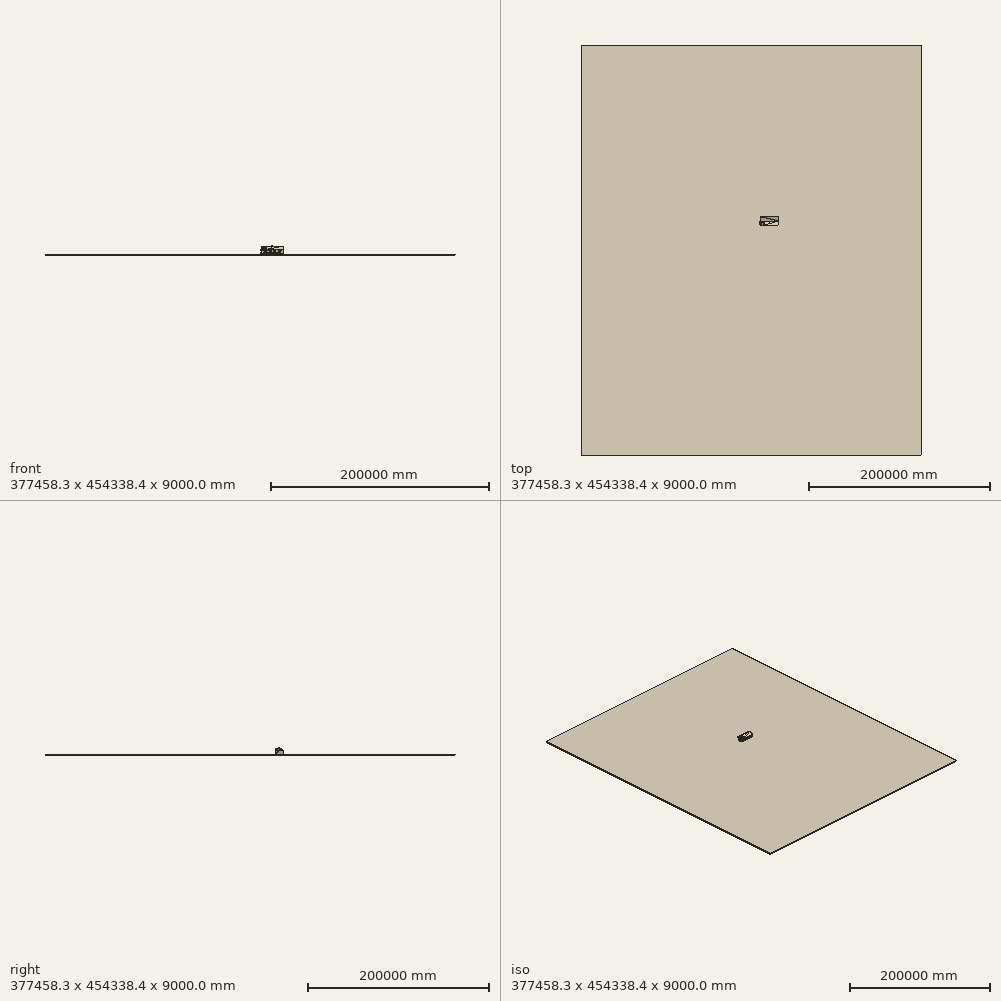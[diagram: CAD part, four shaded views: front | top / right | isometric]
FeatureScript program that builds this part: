
annotation { "Feature Type Name" : "Feature", "Feature Type Description" : "" }
export const myFeature = defineFeature(function(context is Context, id is Id, definition is map)
    precondition{}
    {
        {
            var Q0;
            Q0=qCreatedBy(makeId("Top.planeOp"),FACE);
            var sketch = newSketch(context, id + "F0", { "sketchPlane" : qUnion([Q0])});
            skLineSegment(sketch, "E0.bottom", {"start": v(-10000, 4500) * mm, "end": v(10000, 4500) * mm});
            skLineSegment(sketch, "E0.top", {"start": v(-10000, -4500) * mm, "end": v(10000, -4500) * mm});
            skLineSegment(sketch, "E0.left", {"start": v(-10000, 4500) * mm, "end": v(-10000, -4500) * mm});
            skLineSegment(sketch, "E0.right", {"start": v(10000, 4500) * mm, "end": v(10000, -4500) * mm});
            skLineSegment(sketch, "E1", {"start": v(-10000, 4500) * mm, "end": v(10000, -4500) * mm, "construction": true});
            skSolve(sketch);
        }
        {
            var Q0;
            Q0 = qSketchRegion(id + "F0", true);
            extrude(context, id + "F1", {"entities" : qUnion([Q0]), "depth" : 700 * mm});
        }
        {
            var Q0;
            Q0=qCreatedBy(makeId("Right.planeOp"),FACE);
            var sketch = newSketch(context, id + "F2", { "sketchPlane" : qUnion([Q0])});
            skLineSegment(sketch, "E2", {"start": v(4500, 700) * mm, "end": v(4500, 4201) * mm});
            skLineSegment(sketch, "E3", {"start": v(4500, 4201) * mm, "end": v(0, 7100) * mm});
            skLineSegment(sketch, "E4", {"start": v(0, 7100) * mm, "end": v(-4500, 4201) * mm});
            skLineSegment(sketch, "E5", {"start": v(-4500, 4201) * mm, "end": v(-4500, 700) * mm});
            skLineSegment(sketch, "E6", {"start": v(-4500, 700) * mm, "end": v(4500, 700) * mm});
            skSolve(sketch);
        }
        {
            var Q0;
            Q0 = qSketchRegion(id + "F2", true);
            var Q1;
            Q1=makeQuery(id+"F1.opExtrude","SWEPT_FACE",FACE,{"disambiguationData":[OSD([sQuery(id+"F0.wireOp",EDGE,"E0.right")])]});
            var Q2;
            Q2=makeQuery(id+"F1.opExtrude","SWEPT_FACE",FACE,{"disambiguationData":[OSD([sQuery(id+"F0.wireOp",EDGE,"E0.left")])]});
            extrude(context, id + "F3", {"entities" : qUnion([Q0]), "endBound" : BoundingType.UP_TO_SURFACE, "endBoundEntityFace" : qUnion([Q1]), "depth" : 25 * mm, "hasSecondDirection" : true, "secondDirectionBound" : SecondDirectionBoundingType.UP_TO_SURFACE, "secondDirectionOppositeDirection" : true, "secondDirectionBoundEntityFace" : qUnion([Q2]), "secondDirectionDepth" : 25 * mm});
        }
        {
            var Q0;
            Q0=makeQuery(id+"F3.opExtrude","SWEPT_FACE",FACE,{"disambiguationData":[OSD([sQuery(id+"F2.wireOp",EDGE,"E5")])]});
            var sketch = newSketch(context, id + "F4", { "sketchPlane" : qUnion([Q0])});
            skLineSegment(sketch, "E7.bottom", {"start": v(-7000, 3401) * mm, "end": v(-6325, 3401) * mm});
            skLineSegment(sketch, "E7.top", {"start": v(-7000, 2001) * mm, "end": v(-6325, 2001) * mm});
            skLineSegment(sketch, "E7.left", {"start": v(-7000, 3401) * mm, "end": v(-7000, 2001) * mm});
            skLineSegment(sketch, "E7.right", {"start": v(-6325, 3401) * mm, "end": v(-6325, 2001) * mm});
            skLineSegment(sketch, "E8.bottom", {"start": v(-6275, 3401) * mm, "end": v(-5600, 3401) * mm});
            skLineSegment(sketch, "E8.top", {"start": v(-6275, 2001) * mm, "end": v(-5600, 2001) * mm});
            skLineSegment(sketch, "E8.left", {"start": v(-6275, 3401) * mm, "end": v(-6275, 2001) * mm});
            skLineSegment(sketch, "E8.right", {"start": v(-5600, 3401) * mm, "end": v(-5600, 2001) * mm});
            skLineSegment(sketch, "E9.bottom", {"start": v(-2600, 3401) * mm, "end": v(-1925, 3401) * mm});
            skLineSegment(sketch, "E9.top", {"start": v(-2600, 2001) * mm, "end": v(-1925, 2001) * mm});
            skLineSegment(sketch, "E9.left", {"start": v(-2600, 3401) * mm, "end": v(-2600, 2001) * mm});
            skLineSegment(sketch, "E9.right", {"start": v(-1925, 3401) * mm, "end": v(-1925, 2001) * mm});
            skLineSegment(sketch, "E10.bottom", {"start": v(-1875, 3401) * mm, "end": v(-1200, 3401) * mm});
            skLineSegment(sketch, "E10.top", {"start": v(-1875, 2001) * mm, "end": v(-1200, 2001) * mm});
            skLineSegment(sketch, "E10.left", {"start": v(-1875, 3401) * mm, "end": v(-1875, 2001) * mm});
            skLineSegment(sketch, "E11.bottom", {"start": v(1300, 3401) * mm, "end": v(1975, 3401) * mm});
            skLineSegment(sketch, "E11.top", {"start": v(1300, 2001) * mm, "end": v(1975, 2001) * mm});
            skLineSegment(sketch, "E11.left", {"start": v(1300, 3401) * mm, "end": v(1300, 2001) * mm});
            skLineSegment(sketch, "E11.right", {"start": v(1975, 3401) * mm, "end": v(1975, 2001) * mm});
            skLineSegment(sketch, "E12.bottom", {"start": v(2025, 3401) * mm, "end": v(2700, 3401) * mm});
            skLineSegment(sketch, "E12.top", {"start": v(2025, 2001) * mm, "end": v(2700, 2001) * mm});
            skLineSegment(sketch, "E12.left", {"start": v(2025, 3401) * mm, "end": v(2025, 2001) * mm});
            skLineSegment(sketch, "E12.right", {"start": v(2700, 3401) * mm, "end": v(2700, 2001) * mm});
            skLineSegment(sketch, "E13.bottom", {"start": v(5700, 3401) * mm, "end": v(6375, 3401) * mm});
            skLineSegment(sketch, "E13.top", {"start": v(5700, 2001) * mm, "end": v(6375, 2001) * mm});
            skLineSegment(sketch, "E13.left", {"start": v(5700, 3401) * mm, "end": v(5700, 2001) * mm});
            skLineSegment(sketch, "E13.right", {"start": v(6375, 3401) * mm, "end": v(6375, 2001) * mm});
            skLineSegment(sketch, "E14.bottom", {"start": v(6425, 3401) * mm, "end": v(7100, 3401) * mm});
            skLineSegment(sketch, "E14.top", {"start": v(6425, 2001) * mm, "end": v(7100, 2001) * mm});
            skLineSegment(sketch, "E14.left", {"start": v(6425, 3401) * mm, "end": v(6425, 2001) * mm});
            skLineSegment(sketch, "E14.right", {"start": v(7100, 3401) * mm, "end": v(7100, 2001) * mm});
            skLineSegment(sketch, "E15", {"start": v(-6325, 2701) * mm, "end": v(-6275, 2701) * mm, "construction": true});
            skLineSegment(sketch, "E16", {"start": v(-1925, 2701) * mm, "end": v(-1875, 2701) * mm, "construction": true});
            skLineSegment(sketch, "E17", {"start": v(1975, 2701) * mm, "end": v(2025, 2701) * mm, "construction": true});
            skLineSegment(sketch, "E18", {"start": v(6375, 2701) * mm, "end": v(6425, 2701) * mm, "construction": true});
            skLineSegment(sketch, "E19", {"start": v(-1200, 2001) * mm, "end": v(-1200, 3401) * mm});
            skSolve(sketch);
        }
        {
            var Q0;
            Q0 = qSketchRegion(id + "F4", true);
            extrude(context, id + "F5", {"entities" : qUnion([Q0]), "operationType" : NewBodyOperationType.REMOVE, "oppositeDirection" : true, "depth" : 100 * mm});
        }
        {
            var Q0;
            Q0=qCreatedBy(makeId("Right.planeOp"),FACE);
            var sketch = newSketch(context, id + "F6", { "sketchPlane" : qUnion([Q0])});
            skLineSegment(sketch, "E20", {"start": v(4500, 4201) * mm, "end": v(0, 7100) * mm});
            skLineSegment(sketch, "E21", {"start": v(0, 7100) * mm, "end": v(-4500, 4201) * mm});
            skLineSegment(sketch, "E22", {"start": v(-4977.96, 4131) * mm, "end": v(0, 7337.9) * mm});
            skLineSegment(sketch, "E23", {"start": v(0, 7337.9) * mm, "end": v(4977.96, 4131) * mm});
            skPoint(sketch, "E24", {"position": v(4500, 4201) * mm});
            skLineSegment(sketch, "E25", {"start": v(4500, 4131) * mm, "end": v(4500, 4201) * mm});
            skLineSegment(sketch, "E26", {"start": v(4977.96, 4131) * mm, "end": v(4500, 4131) * mm});
            skLineSegment(sketch, "E27", {"start": v(-4977.96, 4131) * mm, "end": v(-4500, 4131) * mm});
            skLineSegment(sketch, "E28", {"start": v(-4500, 4131) * mm, "end": v(-4500, 4201) * mm});
            skSolve(sketch);
        }
        {
            var Q0;
            Q0 = qSketchRegion(id + "F6", true);
            extrude(context, id + "F7", {"entities" : qUnion([Q0]), "endBound" : BoundingType.SYMMETRIC, "depth" : (20000 + 400) * mm});
        }
        {
            var Q0;
            Q0=makeQuery(id+"F1.opExtrude","CAP_FACE",FACE,{"disambiguationData":[OSD([sQuery(id+"F0.wireOp",EDGE,"E0.bottom"),sQuery(id+"F0.wireOp",EDGE,"E0.top"),sQuery(id+"F0.wireOp",EDGE,"E0.left"),sQuery(id+"F0.wireOp",EDGE,"E0.right")])],"isStart":true});
            var sketch = newSketch(context, id + "F8", { "sketchPlane" : qUnion([Q0])});
            skLineSegment(sketch, "E29.bottom", {"start": v(-300, 1631.99) * mm, "end": v(600, 1631.99) * mm});
            skLineSegment(sketch, "E29.top", {"start": v(-300, 431.99) * mm, "end": v(600, 431.99) * mm});
            skLineSegment(sketch, "E29.left", {"start": v(-300, 1631.99) * mm, "end": v(-300, 431.99) * mm});
            skLineSegment(sketch, "E29.right", {"start": v(600, 1631.99) * mm, "end": v(600, 431.99) * mm});
            skSolve(sketch);
        }
        {
            var Q0;
            Q0 = qSketchRegion(id + "F8", true);
            extrude(context, id + "F9", {"entities" : qUnion([Q0]), "oppositeDirection" : true, "depth" : 8000 * mm});
        }
        {
            var Q0;
            Q0=qCreatedBy(makeId("Front.planeOp"),FACE);
            var sketch = newSketch(context, id + "F10", { "sketchPlane" : qUnion([Q0])});
            skLineSegment(sketch, "E30", {"start": v(-8800, 4201) * mm, "end": v(-5600, 4201) * mm});
            skLineSegment(sketch, "E31", {"start": v(-5600, 4201) * mm, "end": v(-5600, 5855.19) * mm});
            skLineSegment(sketch, "E32", {"start": v(-5600, 5855.19) * mm, "end": v(-7200, 7082.9) * mm});
            skLineSegment(sketch, "E33", {"start": v(-7200, 7082.9) * mm, "end": v(-8800, 5855.19) * mm});
            skLineSegment(sketch, "E34", {"start": v(-8800, 5855.19) * mm, "end": v(-8800, 4201) * mm});
            skSolve(sketch);
        }
        {
            var Q0;
            Q0 = qSketchRegion(id + "F10", true);
            extrude(context, id + "F11", {"entities" : qUnion([Q0]), "depth" : 4500 * mm});
        }
        {
            var Q0;
            Q0=qCreatedBy(makeId("Front.planeOp"),FACE);
            var sketch = newSketch(context, id + "F12", { "sketchPlane" : qUnion([Q0])});
            skLineSegment(sketch, "E35", {"start": v(-9000, 5701.72) * mm, "end": v(-7200, 7082.9) * mm});
            skLineSegment(sketch, "E36", {"start": v(-7200, 7082.9) * mm, "end": v(-5400, 5701.72) * mm});
            skLineSegment(sketch, "E37", {"start": v(-5400, 5701.72) * mm, "end": v(-5278.25, 5860.4) * mm});
            skLineSegment(sketch, "E38", {"start": v(-5278.25, 5860.4) * mm, "end": v(-7200, 7335) * mm});
            skLineSegment(sketch, "E39", {"start": v(-7200, 7335) * mm, "end": v(-9121.75, 5860.4) * mm});
            skLineSegment(sketch, "E40", {"start": v(-9121.75, 5860.4) * mm, "end": v(-9000, 5701.72) * mm});
            skSolve(sketch);
        }
        {
            var Q0;
            Q0 = qSketchRegion(id + "F12", true);
            extrude(context, id + "F13", {"entities" : qUnion([Q0]), "depth" : (4500 + 200) * mm});
        }
        {
            var Q0;
            Q0=makeQuery(id+"F11.opExtrude","CAP_FACE",FACE,{"disambiguationData":[OSD([sQuery(id+"F10.wireOp",EDGE,"E30"),sQuery(id+"F10.wireOp",EDGE,"E31"),sQuery(id+"F10.wireOp",EDGE,"E32"),sQuery(id+"F10.wireOp",EDGE,"E33"),sQuery(id+"F10.wireOp",EDGE,"E34")])],"isStart":false});
            var sketch = newSketch(context, id + "F14", { "sketchPlane" : qUnion([Q0])});
            skLineSegment(sketch, "E41.bottom", {"start": v(-8400, 6082.9) * mm, "end": v(-7400, 6082.9) * mm});
            skLineSegment(sketch, "E41.top", {"start": v(-8400, 4882.9) * mm, "end": v(-7400, 4882.9) * mm});
            skLineSegment(sketch, "E41.left", {"start": v(-8400, 6082.9) * mm, "end": v(-8400, 4882.9) * mm});
            skLineSegment(sketch, "E41.right", {"start": v(-7400, 6082.9) * mm, "end": v(-7400, 4882.9) * mm});
            skLineSegment(sketch, "E42.bottom", {"start": v(-7000, 6082.9) * mm, "end": v(-6000, 6082.9) * mm});
            skLineSegment(sketch, "E42.top", {"start": v(-7000, 4882.9) * mm, "end": v(-6000, 4882.9) * mm});
            skLineSegment(sketch, "E42.left", {"start": v(-7000, 6082.9) * mm, "end": v(-7000, 4882.9) * mm});
            skLineSegment(sketch, "E42.right", {"start": v(-6000, 6082.9) * mm, "end": v(-6000, 4882.9) * mm});
            skLineSegment(sketch, "E43", {"start": v(-7400, 6082.9) * mm, "end": v(-7000, 4882.9) * mm, "construction": true});
            skPoint(sketch, "E44", {"position": v(-7200, 5482.9) * mm});
            skSolve(sketch);
        }
        {
            var Q0;
            Q0 = qSketchRegion(id + "F14", true);
            extrude(context, id + "F15", {"entities" : qUnion([Q0]), "operationType" : NewBodyOperationType.REMOVE, "oppositeDirection" : true, "depth" : 100 * mm});
        }
        {
            var Q0;
            Q0=makeQuery(id+"F1.opExtrude","CAP_FACE",FACE,{"disambiguationData":[OSD([sQuery(id+"F0.wireOp",EDGE,"E0.bottom"),sQuery(id+"F0.wireOp",EDGE,"E0.top"),sQuery(id+"F0.wireOp",EDGE,"E0.left"),sQuery(id+"F0.wireOp",EDGE,"E0.right")])],"isStart":true});
            var sketch = newSketch(context, id + "F16", { "sketchPlane" : qUnion([Q0])});
            skLineSegment(sketch, "E45.bottom", {"start": v(-208724.58, 259754.67) * mm, "end": v(168733.69, 259754.67) * mm});
            skLineSegment(sketch, "E45.top", {"start": v(-208724.58, -194583.7) * mm, "end": v(168733.69, -194583.7) * mm});
            skLineSegment(sketch, "E45.left", {"start": v(-208724.58, 259754.67) * mm, "end": v(-208724.58, -194583.7) * mm});
            skLineSegment(sketch, "E45.right", {"start": v(168733.69, 259754.67) * mm, "end": v(168733.69, -194583.7) * mm});
            skSolve(sketch);
        }
        {
            var Q0;
            Q0 = qSketchRegion(id + "F16", true);
            extrude(context, id + "F17", {"entities" : qUnion([Q0]), "depth" : 1000 * mm});
        }
        {
            var Q0;
            Q0=makeQuery(id+"F3.opExtrude","CAP_FACE",FACE,{"disambiguationData":[OSD([sQuery(id+"F2.wireOp",EDGE,"E2"),sQuery(id+"F2.wireOp",EDGE,"E3"),sQuery(id+"F2.wireOp",EDGE,"E4"),sQuery(id+"F2.wireOp",EDGE,"E5"),sQuery(id+"F2.wireOp",EDGE,"E6")])],"isStart":true});
            var sketch = newSketch(context, id + "F18", { "sketchPlane" : qUnion([Q0])});
            skLineSegment(sketch, "E46.bottom", {"start": v(-700, 5900) * mm, "end": v(-25, 5900) * mm});
            skLineSegment(sketch, "E46.top", {"start": v(-700, 4500) * mm, "end": v(-25, 4500) * mm});
            skLineSegment(sketch, "E46.left", {"start": v(-700, 5900) * mm, "end": v(-700, 4500) * mm});
            skLineSegment(sketch, "E46.right", {"start": v(-25, 5900) * mm, "end": v(-25, 4500) * mm});
            skLineSegment(sketch, "E47.bottom", {"start": v(25, 5900) * mm, "end": v(700, 5900) * mm});
            skLineSegment(sketch, "E47.top", {"start": v(25, 4500) * mm, "end": v(700, 4500) * mm});
            skLineSegment(sketch, "E47.left", {"start": v(25, 5900) * mm, "end": v(25, 4500) * mm});
            skLineSegment(sketch, "E47.right", {"start": v(700, 5900) * mm, "end": v(700, 4500) * mm});
            skLineSegment(sketch, "E48", {"start": v(-25, 5900) * mm, "end": v(25, 4500) * mm, "construction": true});
            skPoint(sketch, "E49", {"position": v(0, 5200) * mm});
            skLineSegment(sketch, "E50.bottom", {"start": v(-3300, 3500) * mm, "end": v(-2625, 3500) * mm});
            skLineSegment(sketch, "E50.top", {"start": v(-3300, 2100) * mm, "end": v(-2625, 2100) * mm});
            skLineSegment(sketch, "E50.left", {"start": v(-3300, 3500) * mm, "end": v(-3300, 2100) * mm});
            skLineSegment(sketch, "E50.right", {"start": v(-2625, 3500) * mm, "end": v(-2625, 2100) * mm});
            skLineSegment(sketch, "E51.bottom", {"start": v(-2575, 3500) * mm, "end": v(-1900, 3500) * mm});
            skLineSegment(sketch, "E51.top", {"start": v(-2575, 2100) * mm, "end": v(-1900, 2100) * mm});
            skLineSegment(sketch, "E51.left", {"start": v(-2575, 3500) * mm, "end": v(-2575, 2100) * mm});
            skLineSegment(sketch, "E51.right", {"start": v(-1900, 3500) * mm, "end": v(-1900, 2100) * mm});
            skLineSegment(sketch, "E52.bottom", {"start": v(3300, 3500) * mm, "end": v(2500, 3500) * mm});
            skLineSegment(sketch, "E52.top", {"start": v(3300, 3000) * mm, "end": v(2500, 3000) * mm});
            skLineSegment(sketch, "E52.left", {"start": v(3300, 3500) * mm, "end": v(3300, 3000) * mm});
            skLineSegment(sketch, "E52.right", {"start": v(2500, 3500) * mm, "end": v(2500, 3000) * mm});
            skLineSegment(sketch, "E53.bottom", {"start": v(600, 3500) * mm, "end": v(1500, 3500) * mm});
            skLineSegment(sketch, "E53.top", {"start": v(600, 1500) * mm, "end": v(1500, 1500) * mm});
            skLineSegment(sketch, "E53.left", {"start": v(600, 3500) * mm, "end": v(600, 1500) * mm});
            skLineSegment(sketch, "E53.right", {"start": v(1500, 3500) * mm, "end": v(1500, 1500) * mm});
            skSolve(sketch);
        }
        {
            var Q0;
            Q0 = qSketchRegion(id + "F18", true);
            extrude(context, id + "F19", {"entities" : qUnion([Q0]), "operationType" : NewBodyOperationType.REMOVE, "oppositeDirection" : true, "depth" : 100 * mm});
        }
        {
            var Q0;
            Q0=makeQuery(id+"F3.opExtrude","CAP_FACE",FACE,{"disambiguationData":[OSD([sQuery(id+"F2.wireOp",EDGE,"E2"),sQuery(id+"F2.wireOp",EDGE,"E3"),sQuery(id+"F2.wireOp",EDGE,"E4"),sQuery(id+"F2.wireOp",EDGE,"E5"),sQuery(id+"F2.wireOp",EDGE,"E6")])],"isStart":false});
            var sketch = newSketch(context, id + "F20", { "sketchPlane" : qUnion([Q0])});
            skLineSegment(sketch, "E54.bottom", {"start": v(-700, 5900) * mm, "end": v(-25, 5900) * mm});
            skLineSegment(sketch, "E54.top", {"start": v(-700, 4500) * mm, "end": v(-25, 4500) * mm});
            skLineSegment(sketch, "E54.left", {"start": v(-700, 5900) * mm, "end": v(-700, 4500) * mm});
            skLineSegment(sketch, "E54.right", {"start": v(-25, 5900) * mm, "end": v(-25, 4500) * mm});
            skLineSegment(sketch, "E55.bottom", {"start": v(25, 5900) * mm, "end": v(700, 5900) * mm});
            skLineSegment(sketch, "E55.top", {"start": v(25, 4500) * mm, "end": v(700, 4500) * mm});
            skLineSegment(sketch, "E55.left", {"start": v(25, 5900) * mm, "end": v(25, 4500) * mm});
            skLineSegment(sketch, "E55.right", {"start": v(700, 5900) * mm, "end": v(700, 4500) * mm});
            skSolve(sketch);
        }
        {
            var Q0;
            Q0 = qSketchRegion(id + "F20", true);
            extrude(context, id + "F21", {"entities" : qUnion([Q0]), "operationType" : NewBodyOperationType.REMOVE, "oppositeDirection" : true, "depth" : 100 * mm});
        }
        {
            var Q0;
            Q0=makeQuery(id+"F1.opExtrude","CAP_FACE",FACE,{"disambiguationData":[OSD([sQuery(id+"F0.wireOp",EDGE,"E0.bottom"),sQuery(id+"F0.wireOp",EDGE,"E0.top"),sQuery(id+"F0.wireOp",EDGE,"E0.left"),sQuery(id+"F0.wireOp",EDGE,"E0.right")])],"isStart":true});
            var sketch = newSketch(context, id + "F22", { "sketchPlane" : qUnion([Q0])});
            skLineSegment(sketch, "E56.bottom", {"start": v(-8800, 4500) * mm, "end": v(-5600, 4500) * mm});
            skLineSegment(sketch, "E56.top", {"start": v(-8800, 6461.58) * mm, "end": v(-5600, 6461.58) * mm});
            skLineSegment(sketch, "E56.left", {"start": v(-8800, 4500) * mm, "end": v(-8800, 6461.58) * mm});
            skLineSegment(sketch, "E56.right", {"start": v(-5600, 4500) * mm, "end": v(-5600, 6461.58) * mm});
            skSolve(sketch);
        }
        {
            var Q0;
            Q0 = qSketchRegion(id + "F22", true);
            extrude(context, id + "F23", {"entities" : qUnion([Q0]), "operationType" : NewBodyOperationType.REMOVE, "oppositeDirection" : true, "depth" : 4750 * mm});
        }
        {
            var Q0;
            Q0=makeQuery(id+"F3.opExtrude","SWEPT_FACE",FACE,{"disambiguationData":[OSD([sQuery(id+"F2.wireOp",EDGE,"E5")])]});
            var sketch = newSketch(context, id + "F24", { "sketchPlane" : qUnion([Q0])});
            skLineSegment(sketch, "E57.bottom", {"start": v(-7000, 3401) * mm, "end": v(-5600, 3401) * mm});
            skLineSegment(sketch, "E57.top", {"start": v(-7000, 2001) * mm, "end": v(-5600, 2001) * mm});
            skLineSegment(sketch, "E57.left", {"start": v(-7000, 3401) * mm, "end": v(-7000, 2001) * mm});
            skLineSegment(sketch, "E57.right", {"start": v(-5600, 3401) * mm, "end": v(-5600, 2001) * mm});
            skLineSegment(sketch, "E58.bottom", {"start": v(-2600, 3401) * mm, "end": v(-1200, 3401) * mm});
            skLineSegment(sketch, "E58.top", {"start": v(-2600, 2001) * mm, "end": v(-1200, 2001) * mm});
            skLineSegment(sketch, "E58.left", {"start": v(-2600, 3401) * mm, "end": v(-2600, 2001) * mm});
            skLineSegment(sketch, "E58.right", {"start": v(-1200, 3401) * mm, "end": v(-1200, 2001) * mm});
            skLineSegment(sketch, "E59.bottom", {"start": v(1300, 3401) * mm, "end": v(2700, 3401) * mm});
            skLineSegment(sketch, "E59.top", {"start": v(1300, 2001) * mm, "end": v(2700, 2001) * mm});
            skLineSegment(sketch, "E59.left", {"start": v(1300, 3401) * mm, "end": v(1300, 2001) * mm});
            skLineSegment(sketch, "E59.right", {"start": v(2700, 3401) * mm, "end": v(2700, 2001) * mm});
            skLineSegment(sketch, "E60.bottom", {"start": v(5700, 3401) * mm, "end": v(7100, 3401) * mm});
            skLineSegment(sketch, "E60.top", {"start": v(5700, 2001) * mm, "end": v(7100, 2001) * mm});
            skLineSegment(sketch, "E60.left", {"start": v(5700, 3401) * mm, "end": v(5700, 2001) * mm});
            skLineSegment(sketch, "E60.right", {"start": v(7100, 3401) * mm, "end": v(7100, 2001) * mm});
            skLineSegment(sketch, "E61.bottom", {"start": v(-7150, 3551) * mm, "end": v(-5450, 3551) * mm});
            skLineSegment(sketch, "E61.top", {"start": v(-7150, 1851) * mm, "end": v(-5450, 1851) * mm});
            skLineSegment(sketch, "E61.left", {"start": v(-7150, 3551) * mm, "end": v(-7150, 1851) * mm});
            skLineSegment(sketch, "E61.right", {"start": v(-5450, 3551) * mm, "end": v(-5450, 1851) * mm});
            skLineSegment(sketch, "E62.bottom", {"start": v(-2750, 3551) * mm, "end": v(-1050, 3551) * mm});
            skLineSegment(sketch, "E62.top", {"start": v(-2750, 1851) * mm, "end": v(-1050, 1851) * mm});
            skLineSegment(sketch, "E62.left", {"start": v(-2750, 3551) * mm, "end": v(-2750, 1851) * mm});
            skLineSegment(sketch, "E62.right", {"start": v(-1050, 3551) * mm, "end": v(-1050, 1851) * mm});
            skLineSegment(sketch, "E63.bottom", {"start": v(1150, 3551) * mm, "end": v(2850, 3551) * mm});
            skLineSegment(sketch, "E63.top", {"start": v(1150, 1851) * mm, "end": v(2850, 1851) * mm});
            skLineSegment(sketch, "E63.left", {"start": v(1150, 3551) * mm, "end": v(1150, 1851) * mm});
            skLineSegment(sketch, "E63.right", {"start": v(2850, 3551) * mm, "end": v(2850, 1851) * mm});
            skLineSegment(sketch, "E64.bottom", {"start": v(5550, 3551) * mm, "end": v(7250, 3551) * mm});
            skLineSegment(sketch, "E64.top", {"start": v(5550, 1851) * mm, "end": v(7250, 1851) * mm});
            skLineSegment(sketch, "E64.left", {"start": v(5550, 3551) * mm, "end": v(5550, 1851) * mm});
            skLineSegment(sketch, "E64.right", {"start": v(7250, 3551) * mm, "end": v(7250, 1851) * mm});
            skLineSegment(sketch, "E65", {"start": v(-2750, 3017.2) * mm, "end": v(-2600, 3017.2) * mm, "construction": true});
            skLineSegment(sketch, "E66", {"start": v(1150, 2950.76) * mm, "end": v(1300, 2950.76) * mm, "construction": true});
            skLineSegment(sketch, "E67", {"start": v(5550, 2891.3) * mm, "end": v(5700, 2891.3) * mm, "construction": true});
            skLineSegment(sketch, "E68", {"start": v(-7150, 3050.06) * mm, "end": v(-7000, 3050.06) * mm, "construction": true});
            skLineSegment(sketch, "E69.bottom", {"start": v(-8400, 6082.9) * mm, "end": v(-7400, 6082.9) * mm});
            skLineSegment(sketch, "E69.top", {"start": v(-8400, 4882.9) * mm, "end": v(-7400, 4882.9) * mm});
            skLineSegment(sketch, "E69.left", {"start": v(-8400, 6082.9) * mm, "end": v(-8400, 4882.9) * mm});
            skLineSegment(sketch, "E69.right", {"start": v(-6000, 6082.9) * mm, "end": v(-6000, 4882.9) * mm});
            skLineSegment(sketch, "E70.bottom", {"start": v(-8500, 6182.9) * mm, "end": v(-7300, 6182.9) * mm});
            skLineSegment(sketch, "E70.top", {"start": v(-8500, 4782.9) * mm, "end": v(-7300, 4782.9) * mm});
            skLineSegment(sketch, "E70.left", {"start": v(-8500, 6182.9) * mm, "end": v(-8500, 4782.9) * mm});
            skLineSegment(sketch, "E70.right", {"start": v(-5900, 6182.9) * mm, "end": v(-5900, 4782.9) * mm});
            skLineSegment(sketch, "E71", {"start": v(-8500, 5317.96) * mm, "end": v(-8400, 5317.96) * mm, "construction": true});
            skLineSegment(sketch, "E72", {"start": v(-6736.92, 4882.9) * mm, "end": v(-6736.92, 4782.9) * mm, "construction": true});
            skPoint(sketch, "E72.endSnap0", {"position": v(-7200, 4782.9) * mm});
            skLineSegment(sketch, "E73", {"start": v(-7200, 6082.9) * mm, "end": v(-7200, 6182.9) * mm, "construction": true});
            skLineSegment(sketch, "E74", {"start": v(-6000, 5482.9) * mm, "end": v(-5900, 5482.9) * mm, "construction": true});
            skLineSegment(sketch, "E75", {"start": v(-7400, 6082.9) * mm, "end": v(-7400, 4882.9) * mm});
            skLineSegment(sketch, "E76", {"start": v(-7000, 4882.9) * mm, "end": v(-7000, 6082.9) * mm});
            skLineSegment(sketch, "E77.trimOffspring", {"start": v(-7000, 6082.9) * mm, "end": v(-6000, 6082.9) * mm});
            skLineSegment(sketch, "E78.trimOffspring", {"start": v(-7000, 4882.9) * mm, "end": v(-6000, 4882.9) * mm});
            skLineSegment(sketch, "E79", {"start": v(-7300, 4782.9) * mm, "end": v(-7300, 6182.9) * mm});
            skLineSegment(sketch, "E80", {"start": v(-7100, 6182.9) * mm, "end": v(-7100, 4782.9) * mm});
            skLineSegment(sketch, "E81.trimOffspring", {"start": v(-7100, 6182.9) * mm, "end": v(-5900, 6182.9) * mm});
            skLineSegment(sketch, "E82.trimOffspring", {"start": v(-7100, 4782.9) * mm, "end": v(-5900, 4782.9) * mm});
            skLineSegment(sketch, "E83", {"start": v(-7400, 5348.24) * mm, "end": v(-7300, 5348.24) * mm, "construction": true});
            skLineSegment(sketch, "E84", {"start": v(-7100, 5324.94) * mm, "end": v(-7000, 5324.94) * mm, "construction": true});
            skSolve(sketch);
        }
        {
            var Q0;
            Q0 = qSketchRegion(id + "F24", true);
            extrude(context, id + "F25", {"entities" : qUnion([Q0]), "depth" : 2 * mm});
        }
        {
            var Q0;
            Q0=makeQuery(id+"F3.opExtrude","CAP_FACE",FACE,{"disambiguationData":[OSD([sQuery(id+"F2.wireOp",EDGE,"E2"),sQuery(id+"F2.wireOp",EDGE,"E3"),sQuery(id+"F2.wireOp",EDGE,"E4"),sQuery(id+"F2.wireOp",EDGE,"E5"),sQuery(id+"F2.wireOp",EDGE,"E6")])],"isStart":true});
            var sketch = newSketch(context, id + "F26", { "sketchPlane" : qUnion([Q0])});
            skLineSegment(sketch, "E85.bottom", {"start": v(-700, 5900) * mm, "end": v(700, 5900) * mm});
            skLineSegment(sketch, "E85.top", {"start": v(-700, 4500) * mm, "end": v(700, 4500) * mm});
            skLineSegment(sketch, "E85.left", {"start": v(-700, 5900) * mm, "end": v(-700, 4500) * mm});
            skLineSegment(sketch, "E85.right", {"start": v(700, 5900) * mm, "end": v(700, 4500) * mm});
            skLineSegment(sketch, "E86.bottom", {"start": v(-850, 6050) * mm, "end": v(850, 6050) * mm});
            skLineSegment(sketch, "E86.top", {"start": v(-850, 4350) * mm, "end": v(850, 4350) * mm});
            skLineSegment(sketch, "E86.left", {"start": v(-850, 6050) * mm, "end": v(-850, 4350) * mm});
            skLineSegment(sketch, "E86.right", {"start": v(850, 6050) * mm, "end": v(850, 4350) * mm});
            skLineSegment(sketch, "E87.bottom", {"start": v(-3300, 3500) * mm, "end": v(-1900, 3500) * mm});
            skLineSegment(sketch, "E87.top", {"start": v(-3300, 2100) * mm, "end": v(-1900, 2100) * mm});
            skLineSegment(sketch, "E87.left", {"start": v(-3300, 3500) * mm, "end": v(-3300, 2100) * mm});
            skLineSegment(sketch, "E87.right", {"start": v(-1900, 3500) * mm, "end": v(-1900, 2100) * mm});
            skLineSegment(sketch, "E88.bottom", {"start": v(-3450, 3650) * mm, "end": v(-1750, 3650) * mm});
            skLineSegment(sketch, "E88.top", {"start": v(-3450, 1950) * mm, "end": v(-1750, 1950) * mm});
            skLineSegment(sketch, "E88.left", {"start": v(-3450, 3650) * mm, "end": v(-3450, 1950) * mm});
            skLineSegment(sketch, "E88.right", {"start": v(-1750, 3650) * mm, "end": v(-1750, 1950) * mm});
            skLineSegment(sketch, "E89.bottom", {"start": v(600, 3500) * mm, "end": v(1500, 3500) * mm});
            skLineSegment(sketch, "E89.top", {"start": v(600, 1500) * mm, "end": v(1500, 1500) * mm});
            skLineSegment(sketch, "E89.left", {"start": v(600, 3500) * mm, "end": v(600, 1500) * mm});
            skLineSegment(sketch, "E89.right", {"start": v(1500, 3500) * mm, "end": v(1500, 1500) * mm});
            skLineSegment(sketch, "E90.bottom", {"start": v(450, 3650) * mm, "end": v(1650, 3650) * mm});
            skLineSegment(sketch, "E90.top", {"start": v(450, 1350) * mm, "end": v(1650, 1350) * mm});
            skLineSegment(sketch, "E90.left", {"start": v(450, 3650) * mm, "end": v(450, 1350) * mm});
            skLineSegment(sketch, "E90.right", {"start": v(1650, 3650) * mm, "end": v(1650, 1350) * mm});
            skLineSegment(sketch, "E91.bottom", {"start": v(2500, 3500) * mm, "end": v(3300, 3500) * mm});
            skLineSegment(sketch, "E91.top", {"start": v(2500, 3000) * mm, "end": v(3300, 3000) * mm});
            skLineSegment(sketch, "E91.left", {"start": v(2500, 3500) * mm, "end": v(2500, 3000) * mm});
            skLineSegment(sketch, "E91.right", {"start": v(3300, 3500) * mm, "end": v(3300, 3000) * mm});
            skLineSegment(sketch, "E92.bottom", {"start": v(2350, 3650) * mm, "end": v(3450, 3650) * mm});
            skLineSegment(sketch, "E92.top", {"start": v(2350, 2850) * mm, "end": v(3450, 2850) * mm});
            skLineSegment(sketch, "E92.left", {"start": v(2350, 3650) * mm, "end": v(2350, 2850) * mm});
            skLineSegment(sketch, "E92.right", {"start": v(3450, 3650) * mm, "end": v(3450, 2850) * mm});
            skLineSegment(sketch, "E93", {"start": v(-3450, 3650) * mm, "end": v(-1750, 1950) * mm, "construction": true});
            skLineSegment(sketch, "E94", {"start": v(-3300, 2100) * mm, "end": v(-1900, 3500) * mm, "construction": true});
            skLineSegment(sketch, "E95", {"start": v(600, 3500) * mm, "end": v(1500, 1500) * mm, "construction": true});
            skLineSegment(sketch, "E96", {"start": v(450, 1350) * mm, "end": v(1650, 3650) * mm, "construction": true});
            skLineSegment(sketch, "E97", {"start": v(2500, 3500) * mm, "end": v(3300, 3000) * mm, "construction": true});
            skLineSegment(sketch, "E98", {"start": v(2350, 2850) * mm, "end": v(3450, 3650) * mm, "construction": true});
            skLineSegment(sketch, "E99", {"start": v(850, 4350) * mm, "end": v(-850, 6050) * mm, "construction": true});
            skLineSegment(sketch, "E100", {"start": v(-700, 4500) * mm, "end": v(700, 5900) * mm, "construction": true});
            skPoint(sketch, "E101", {"position": v(-2600, 2800) * mm});
            skPoint(sketch, "E102", {"position": v(1050, 2500) * mm});
            skPoint(sketch, "E103", {"position": v(0, 5200) * mm});
            skPoint(sketch, "E104", {"position": v(2900, 3250) * mm});
            skLineSegment(sketch, "E105", {"start": v(450, 2628.66) * mm, "end": v(600, 2628.66) * mm, "construction": true});
            skLineSegment(sketch, "E106", {"start": v(2350, 3250) * mm, "end": v(2500, 3250) * mm, "construction": true});
            skLineSegment(sketch, "E107", {"start": v(-3450, 3001.79) * mm, "end": v(-3300, 3001.79) * mm, "construction": true});
            skSolve(sketch);
        }
        {
            var Q0;
            Q0 = qSketchRegion(id + "F26", true);
            extrude(context, id + "F27", {"entities" : qUnion([Q0]), "depth" : 2 * mm});
        }
        {
            var Q0;
            Q0=makeQuery(id+"F19.boolean.opBoolean","COPY",FACE,{"derivedFrom":makeQuery(id+"F19.opExtrude","CAP_FACE",FACE,{"disambiguationData":[OSD([sQuery(id+"F18.wireOp",EDGE,"E53.bottom"),sQuery(id+"F18.wireOp",EDGE,"E53.top"),sQuery(id+"F18.wireOp",EDGE,"E53.left"),sQuery(id+"F18.wireOp",EDGE,"E53.right")])],"isStart":false})});
            var sketch = newSketch(context, id + "F28", { "sketchPlane" : qUnion([Q0])});
            skLineSegment(sketch, "E108.bottom", {"start": v(600, 3500) * mm, "end": v(1500, 3500) * mm});
            skLineSegment(sketch, "E108.top", {"start": v(600, 1500) * mm, "end": v(1500, 1500) * mm});
            skLineSegment(sketch, "E108.left", {"start": v(600, 3500) * mm, "end": v(600, 1500) * mm});
            skLineSegment(sketch, "E108.right", {"start": v(1500, 3500) * mm, "end": v(1500, 1500) * mm});
            skSolve(sketch);
        }
        {
            var Q0;
            Q0 = qSketchRegion(id + "F28", true);
            extrude(context, id + "F29", {"entities" : qUnion([Q0]), "depth" : 2 * mm});
        }
        {
            var Q0;
            Q0=makeQuery(id+"F5.boolean.opBoolean","COPY",FACE,{"derivedFrom":makeQuery(id+"F5.opExtrude","CAP_FACE",FACE,{"disambiguationData":[OSD([sQuery(id+"F4.wireOp",EDGE,"E7.bottom"),sQuery(id+"F4.wireOp",EDGE,"E7.top"),sQuery(id+"F4.wireOp",EDGE,"E7.left"),sQuery(id+"F4.wireOp",EDGE,"E7.right")])],"isStart":false})});
            var sketch = newSketch(context, id + "F30", { "sketchPlane" : qUnion([Q0])});
            skLineSegment(sketch, "E109.bottom", {"start": v(-7000, 3401) * mm, "end": v(-6325, 3401) * mm});
            skLineSegment(sketch, "E109.top", {"start": v(-7000, 2001) * mm, "end": v(-6325, 2001) * mm});
            skLineSegment(sketch, "E109.left", {"start": v(-7000, 3401) * mm, "end": v(-7000, 2001) * mm});
            skLineSegment(sketch, "E109.right", {"start": v(-6325, 3401) * mm, "end": v(-6325, 2001) * mm});
            skLineSegment(sketch, "E110.bottom", {"start": v(-6275, 3401) * mm, "end": v(-5600, 3401) * mm});
            skLineSegment(sketch, "E110.top", {"start": v(-6275, 2001) * mm, "end": v(-5600, 2001) * mm});
            skLineSegment(sketch, "E110.left", {"start": v(-6275, 3401) * mm, "end": v(-6275, 2001) * mm});
            skLineSegment(sketch, "E110.right", {"start": v(-5600, 3401) * mm, "end": v(-5600, 2001) * mm});
            skLineSegment(sketch, "E111.bottom", {"start": v(-2600, 3401) * mm, "end": v(-1925, 3401) * mm});
            skLineSegment(sketch, "E111.top", {"start": v(-2600, 2001) * mm, "end": v(-1925, 2001) * mm});
            skLineSegment(sketch, "E111.left", {"start": v(-2600, 3401) * mm, "end": v(-2600, 2001) * mm});
            skLineSegment(sketch, "E111.right", {"start": v(-1925, 3401) * mm, "end": v(-1925, 2001) * mm});
            skLineSegment(sketch, "E112.bottom", {"start": v(-1875, 3401) * mm, "end": v(-1200, 3401) * mm});
            skLineSegment(sketch, "E112.top", {"start": v(-1875, 2001) * mm, "end": v(-1200, 2001) * mm});
            skLineSegment(sketch, "E112.left", {"start": v(-1875, 3401) * mm, "end": v(-1875, 2001) * mm});
            skLineSegment(sketch, "E112.right", {"start": v(-1200, 3401) * mm, "end": v(-1200, 2001) * mm});
            skLineSegment(sketch, "E113.bottom", {"start": v(1300, 3401) * mm, "end": v(1975, 3401) * mm});
            skLineSegment(sketch, "E113.top", {"start": v(1300, 2001) * mm, "end": v(1975, 2001) * mm});
            skLineSegment(sketch, "E113.left", {"start": v(1300, 3401) * mm, "end": v(1300, 2001) * mm});
            skLineSegment(sketch, "E113.right", {"start": v(1975, 3401) * mm, "end": v(1975, 2001) * mm});
            skLineSegment(sketch, "E114.bottom", {"start": v(2025, 3401) * mm, "end": v(2700, 3401) * mm});
            skLineSegment(sketch, "E114.top", {"start": v(2025, 2001) * mm, "end": v(2700, 2001) * mm});
            skLineSegment(sketch, "E114.left", {"start": v(2025, 3401) * mm, "end": v(2025, 2001) * mm});
            skLineSegment(sketch, "E114.right", {"start": v(2700, 3401) * mm, "end": v(2700, 2001) * mm});
            skLineSegment(sketch, "E115.bottom", {"start": v(5700, 3401) * mm, "end": v(6375, 3401) * mm});
            skLineSegment(sketch, "E115.top", {"start": v(5700, 2001) * mm, "end": v(6375, 2001) * mm});
            skLineSegment(sketch, "E115.left", {"start": v(5700, 3401) * mm, "end": v(5700, 2001) * mm});
            skLineSegment(sketch, "E115.right", {"start": v(6375, 3401) * mm, "end": v(6375, 2001) * mm});
            skLineSegment(sketch, "E116.bottom", {"start": v(6425, 3401) * mm, "end": v(7100, 3401) * mm});
            skLineSegment(sketch, "E116.top", {"start": v(6425, 2001) * mm, "end": v(7100, 2001) * mm});
            skLineSegment(sketch, "E116.left", {"start": v(6425, 3401) * mm, "end": v(6425, 2001) * mm});
            skLineSegment(sketch, "E116.right", {"start": v(7100, 3401) * mm, "end": v(7100, 2001) * mm});
            skLineSegment(sketch, "E117.bottom", {"start": v(-8400, 6082.9) * mm, "end": v(-7400, 6082.9) * mm});
            skLineSegment(sketch, "E117.top", {"start": v(-8400, 4882.9) * mm, "end": v(-7400, 4882.9) * mm});
            skLineSegment(sketch, "E117.left", {"start": v(-8400, 6082.9) * mm, "end": v(-8400, 4882.9) * mm});
            skLineSegment(sketch, "E117.right", {"start": v(-7400, 6082.9) * mm, "end": v(-7400, 4882.9) * mm});
            skLineSegment(sketch, "E118.bottom", {"start": v(-7000, 6082.9) * mm, "end": v(-6000, 6082.9) * mm});
            skLineSegment(sketch, "E118.top", {"start": v(-7000, 4882.9) * mm, "end": v(-6000, 4882.9) * mm});
            skLineSegment(sketch, "E118.left", {"start": v(-7000, 6082.9) * mm, "end": v(-7000, 4882.9) * mm});
            skLineSegment(sketch, "E118.right", {"start": v(-6000, 6082.9) * mm, "end": v(-6000, 4882.9) * mm});
            skSolve(sketch);
        }
        {
            var Q0;
            Q0 = qSketchRegion(id + "F30", true);
            extrude(context, id + "F31", {"entities" : qUnion([Q0]), "depth" : 2 * mm});
        }
        {
            var Q0;
            Q0 = qSketchRegion(id + "F30", true);
            extrude(context, id + "F32", {"entities" : qUnion([Q0]), "depth" : 2 * mm});
        }
        {
            var Q0;
            Q0=makeQuery(id+"F19.boolean.opBoolean","COPY",FACE,{"derivedFrom":makeQuery(id+"F19.opExtrude","CAP_FACE",FACE,{"disambiguationData":[OSD([sQuery(id+"F18.wireOp",EDGE,"E50.bottom"),sQuery(id+"F18.wireOp",EDGE,"E50.top"),sQuery(id+"F18.wireOp",EDGE,"E50.left"),sQuery(id+"F18.wireOp",EDGE,"E50.right")])],"isStart":false})});
            var sketch = newSketch(context, id + "F33", { "sketchPlane" : qUnion([Q0])});
            skLineSegment(sketch, "E119.bottom", {"start": v(-3300, 3500) * mm, "end": v(-2625, 3500) * mm});
            skLineSegment(sketch, "E119.top", {"start": v(-3300, 2100) * mm, "end": v(-2625, 2100) * mm});
            skLineSegment(sketch, "E119.left", {"start": v(-3300, 3500) * mm, "end": v(-3300, 2100) * mm});
            skLineSegment(sketch, "E119.right", {"start": v(-2625, 3500) * mm, "end": v(-2625, 2100) * mm});
            skLineSegment(sketch, "E120.bottom", {"start": v(-2575, 3500) * mm, "end": v(-1900, 3500) * mm});
            skLineSegment(sketch, "E120.top", {"start": v(-2575, 2100) * mm, "end": v(-1900, 2100) * mm});
            skLineSegment(sketch, "E120.left", {"start": v(-2575, 3500) * mm, "end": v(-2575, 2100) * mm});
            skLineSegment(sketch, "E120.right", {"start": v(-1900, 3500) * mm, "end": v(-1900, 2100) * mm});
            skLineSegment(sketch, "E121.bottom", {"start": v(-700, 5900) * mm, "end": v(-25, 5900) * mm});
            skLineSegment(sketch, "E121.top", {"start": v(-700, 4500) * mm, "end": v(-25, 4500) * mm});
            skLineSegment(sketch, "E121.left", {"start": v(-700, 5900) * mm, "end": v(-700, 4500) * mm});
            skLineSegment(sketch, "E121.right", {"start": v(-25, 5900) * mm, "end": v(-25, 4500) * mm});
            skLineSegment(sketch, "E122.bottom", {"start": v(25, 5900) * mm, "end": v(700, 5900) * mm});
            skLineSegment(sketch, "E122.top", {"start": v(25, 4500) * mm, "end": v(700, 4500) * mm});
            skLineSegment(sketch, "E122.left", {"start": v(25, 5900) * mm, "end": v(25, 4500) * mm});
            skLineSegment(sketch, "E122.right", {"start": v(700, 5900) * mm, "end": v(700, 4500) * mm});
            skLineSegment(sketch, "E123.bottom", {"start": v(2500, 3500) * mm, "end": v(3300, 3500) * mm});
            skLineSegment(sketch, "E123.top", {"start": v(2500, 3000) * mm, "end": v(3300, 3000) * mm});
            skLineSegment(sketch, "E123.left", {"start": v(2500, 3500) * mm, "end": v(2500, 3000) * mm});
            skLineSegment(sketch, "E123.right", {"start": v(3300, 3500) * mm, "end": v(3300, 3000) * mm});
            skSolve(sketch);
        }
        {
            var Q0;
            Q0 = qSketchRegion(id + "F33", true);
            extrude(context, id + "F34", {"entities" : qUnion([Q0]), "depth" : 2 * mm});
        }
        {
            var Q0;
            Q0=makeQuery(id+"F3.opExtrude","CAP_FACE",FACE,{"disambiguationData":[OSD([sQuery(id+"F2.wireOp",EDGE,"E2"),sQuery(id+"F2.wireOp",EDGE,"E3"),sQuery(id+"F2.wireOp",EDGE,"E4"),sQuery(id+"F2.wireOp",EDGE,"E5"),sQuery(id+"F2.wireOp",EDGE,"E6")])],"isStart":true});
            var sketch = newSketch(context, id + "F35", { "sketchPlane" : qUnion([Q0])});
            skLineSegment(sketch, "E124", {"start": v(200, 0) * mm, "end": v(200, 1500) * mm});
            skLineSegment(sketch, "E125", {"start": v(200, 1500) * mm, "end": v(1900, 1500) * mm});
            skLineSegment(sketch, "E126", {"start": v(1900, 1500) * mm, "end": v(1900, 1200) * mm});
            skLineSegment(sketch, "E127", {"start": v(1900, 1200) * mm, "end": v(2400, 1200) * mm});
            skLineSegment(sketch, "E128", {"start": v(2400, 1200) * mm, "end": v(2400, 900) * mm});
            skLineSegment(sketch, "E129", {"start": v(2400, 900) * mm, "end": v(2900, 900) * mm});
            skLineSegment(sketch, "E130", {"start": v(2900, 900) * mm, "end": v(2900, 600) * mm});
            skLineSegment(sketch, "E131", {"start": v(2900, 600) * mm, "end": v(3400, 600) * mm});
            skLineSegment(sketch, "E132", {"start": v(3400, 600) * mm, "end": v(3400, 300) * mm});
            skLineSegment(sketch, "E133", {"start": v(3400, 300) * mm, "end": v(3900, 300) * mm});
            skLineSegment(sketch, "E134", {"start": v(3900, 300) * mm, "end": v(3900, 0) * mm});
            skLineSegment(sketch, "E135", {"start": v(3900, 0) * mm, "end": v(200, 0) * mm});
            skSolve(sketch);
        }
        {
            var Q0;
            Q0 = qSketchRegion(id + "F35", true);
            extrude(context, id + "F36", {"entities" : qUnion([Q0]), "depth" : 1100 * mm});
        }
        {
            var Q0;
            Q0=makeQuery(id+"F3.opExtrude","CAP_FACE",FACE,{"disambiguationData":[OSD([sQuery(id+"F2.wireOp",EDGE,"E2"),sQuery(id+"F2.wireOp",EDGE,"E3"),sQuery(id+"F2.wireOp",EDGE,"E4"),sQuery(id+"F2.wireOp",EDGE,"E5"),sQuery(id+"F2.wireOp",EDGE,"E6")])],"isStart":true});
            var sketch = newSketch(context, id + "F37", { "sketchPlane" : qUnion([Q0])});
            skLineSegment(sketch, "E136", {"start": v(1050, 4450) * mm, "end": v(-100, 3450) * mm});
            skLineSegment(sketch, "E137", {"start": v(2200, 3450) * mm, "end": v(1050, 4450) * mm});
            skPoint(sketch, "E138", {"position": v(1050, 3500) * mm});
            skPoint(sketch, "E139", {"position": v(1050, 3670) * mm});
            skLineSegment(sketch, "E140", {"start": v(-100, 3450) * mm, "end": v(400, 3450) * mm});
            skLineSegment(sketch, "E141", {"start": v(400, 3600) * mm, "end": v(1700, 3600) * mm});
            skLineSegment(sketch, "E142", {"start": v(1700, 3450) * mm, "end": v(2200, 3450) * mm});
            skLineSegment(sketch, "E143", {"start": v(400, 3600) * mm, "end": v(400, 3450) * mm});
            skLineSegment(sketch, "E144", {"start": v(1700, 3600) * mm, "end": v(1700, 3450) * mm});
            skSolve(sketch);
        }
        {
            var Q0;
            Q0 = qSketchRegion(id + "F37", true);
            extrude(context, id + "F38", {"entities" : qUnion([Q0]), "depth" : 1200 * mm});
        }
        {
            var Q0;
            Q0=makeQuery(id+"F1.opExtrude","SWEPT_FACE",FACE,{"disambiguationData":[OSD([sQuery(id+"F0.wireOp",EDGE,"E0.top")])]});
            var sketch = newSketch(context, id + "F39", { "sketchPlane" : qUnion([Q0])});
            skLineSegment(sketch, "E145.bottom", {"start": v(-7100, 500) * mm, "end": v(-6300, 500) * mm});
            skLineSegment(sketch, "E145.top", {"start": v(-7100, 100) * mm, "end": v(-6300, 100) * mm});
            skLineSegment(sketch, "E145.left", {"start": v(-7100, 500) * mm, "end": v(-7100, 100) * mm});
            skLineSegment(sketch, "E145.right", {"start": v(-6300, 500) * mm, "end": v(-6300, 100) * mm});
            skLineSegment(sketch, "E146.bottom", {"start": v(-2400, 500) * mm, "end": v(-1600, 500) * mm});
            skLineSegment(sketch, "E146.top", {"start": v(-2400, 100) * mm, "end": v(-1600, 100) * mm});
            skLineSegment(sketch, "E146.left", {"start": v(-2400, 500) * mm, "end": v(-2400, 100) * mm});
            skLineSegment(sketch, "E146.right", {"start": v(-1600, 500) * mm, "end": v(-1600, 100) * mm});
            skLineSegment(sketch, "E147.bottom", {"start": v(1576.44, 500) * mm, "end": v(2376.44, 500) * mm});
            skLineSegment(sketch, "E147.top", {"start": v(1576.44, 100) * mm, "end": v(2376.44, 100) * mm});
            skLineSegment(sketch, "E147.left", {"start": v(1576.44, 500) * mm, "end": v(1576.44, 100) * mm});
            skLineSegment(sketch, "E147.right", {"start": v(2376.44, 500) * mm, "end": v(2376.44, 100) * mm});
            skLineSegment(sketch, "E148.bottom", {"start": v(5780.37, 500) * mm, "end": v(6580.37, 500) * mm});
            skLineSegment(sketch, "E148.top", {"start": v(5780.37, 100) * mm, "end": v(6580.37, 100) * mm});
            skLineSegment(sketch, "E148.left", {"start": v(5780.37, 500) * mm, "end": v(5780.37, 100) * mm});
            skLineSegment(sketch, "E148.right", {"start": v(6580.37, 500) * mm, "end": v(6580.37, 100) * mm});
            skSolve(sketch);
        }
        {
            var Q0;
            Q0 = qSketchRegion(id + "F39", true);
            extrude(context, id + "F40", {"entities" : qUnion([Q0]), "operationType" : NewBodyOperationType.REMOVE, "oppositeDirection" : true, "depth" : 100 * mm});
        }
    });
